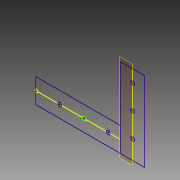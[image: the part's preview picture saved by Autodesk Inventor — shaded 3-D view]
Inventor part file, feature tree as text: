
AUTODESK INVENTOR PART (.ipt)
format: ipt  version: 2014 (Build 180170000, 170)  size: 121,344 bytes
history: native  units: in
note: dims shown in document units (in); Inventor stores cm internally (conversion verified against a paired STEP export)
features: reference x4, plane x1, sheet_metal_op x1, chamfer x1, sketch x1, other x1
ambient origin geometry x8: Origin, YZ Plane, XZ Plane, XY Plane, X Axis, Y Axis, Z Axis, Center Point
bodies: Solid1 (feature_tree)
feature tree (9):
  plane  "Work Plane1"
  sheet_metal_op  "Face1"
  chamfer  "Corner Round1"
  sketch  "Sketch1"  dims[d0=0.125in d1=0.25in]
  reference  "Reference1"
  reference  "Reference2"
  reference  "Reference3"
  reference  "Reference4"
  other  "Plate1"
